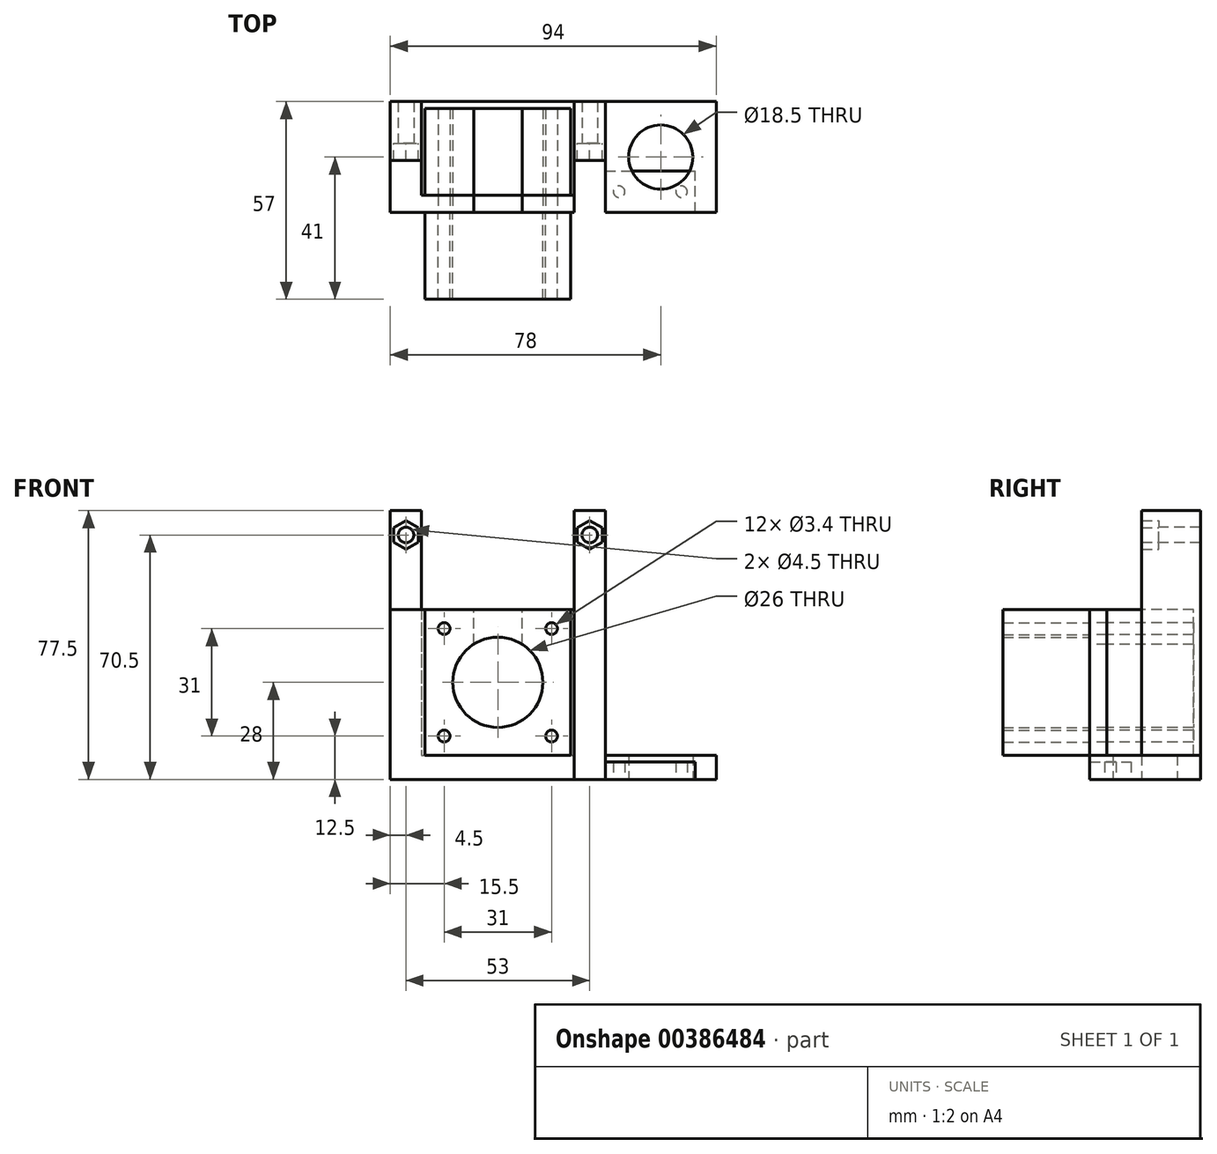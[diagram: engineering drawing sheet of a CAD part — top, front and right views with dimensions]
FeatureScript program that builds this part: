
annotation { "Feature Type Name" : "Feature", "Feature Type Description" : "" }
export const myFeature = defineFeature(function(context is Context, id is Id, definition is map)
    precondition{}
    {
        {
            assignVariable(context, id + "F0", {"name" : "MotorLength", "anyValue" : 25});
        }
        {
            var Q0;
            Q0=qCreatedBy(makeId("Front.planeOp"),FACE);
            var sketch = newSketch(context, id + "F1", { "sketchPlane" : qUnion([Q0])});
            skCircle(sketch, "E0", {"center": v(0, 0) * mm, "radius": 2.25 * mm});
            skCircle(sketch, "E1", {"center": v(-31.5, 49.5) * mm, "radius": 2.25 * mm});
            skCircle(sketch, "E2", {"center": v(21.5, 49.5) * mm, "radius": 2.25 * mm});
            skPoint(sketch, "E3", {"position": v(-36, 56.5) * mm});
            skPoint(sketch, "E4", {"position": v(-27, 56.5) * mm});
            skPoint(sketch, "E5", {"position": v(-27, -14) * mm});
            skLineSegment(sketch, "E6", {"start": v(-36, 56.5) * mm, "end": v(-27, 56.5) * mm});
            skLineSegment(sketch, "E7", {"start": v(-27, 56.5) * mm, "end": v(-27, -14) * mm});
            skLineSegment(sketch, "E8", {"start": v(-27, -14) * mm, "end": v(17, -14) * mm});
            skLineSegment(sketch, "E9", {"start": v(17, -14) * mm, "end": v(17, 56.5) * mm});
            skLineSegment(sketch, "E10", {"start": v(17, 56.5) * mm, "end": v(26, 56.5) * mm});
            skPoint(sketch, "E11", {"position": v(-36, -21) * mm});
            skLineSegment(sketch, "E12", {"start": v(-36, 56.5) * mm, "end": v(-36, -21) * mm});
            skLineSegment(sketch, "E13", {"start": v(-36, -21) * mm, "end": v(26, -21) * mm});
            skLineSegment(sketch, "E14", {"start": v(26, 56.5) * mm, "end": v(26, -21) * mm});
            skSolve(sketch);
        }
        {
            var Q0;
            Q0=makeQuery(id+"F1.imprint","IMPRINT",FACE,{"disambiguationData":[TD([[makeQuery(id+"F1.imprint","IMPRINT",EDGE,{"derivedFrom":sQuery(id+"F1.wireOp",EDGE,"E1")}),-1.0]])]});
            extrude(context, id + "F2", {"entities" : qUnion([Q0]), "oppositeDirection" : true, "depth" : 12 * mm});
        }
        {
            var Q0;
            Q0=makeQuery(id+"F2.opExtrude","CAP_FACE",FACE,{"disambiguationData":[OSD([sQuery(id+"F1.wireOp",EDGE,"E1"),sQuery(id+"F1.wireOp",EDGE,"E2"),sQuery(id+"F1.wireOp",EDGE,"E6"),sQuery(id+"F1.wireOp",EDGE,"E7"),sQuery(id+"F1.wireOp",EDGE,"E8"),sQuery(id+"F1.wireOp",EDGE,"E9"),sQuery(id+"F1.wireOp",EDGE,"E10"),sQuery(id+"F1.wireOp",EDGE,"E12"),sQuery(id+"F1.wireOp",EDGE,"E13"),sQuery(id+"F1.wireOp",EDGE,"E14")])],"isStart":true});
            var sketch = newSketch(context, id + "F3", { "sketchPlane" : qUnion([Q0])});
            skCircle(sketch, "E15.cCircle", {"center": v(-31.5, 49.5) * mm, "radius": 3.6 * mm, "construction": true});
            skLineSegment(sketch, "E15.0", {"start": v(-27.9, 51.58) * mm, "end": v(-27.9, 47.42) * mm});
            skLineSegment(sketch, "E15.1", {"start": v(-27.9, 47.42) * mm, "end": v(-31.5, 45.34) * mm});
            skLineSegment(sketch, "E15.2", {"start": v(-31.5, 45.34) * mm, "end": v(-35.1, 47.42) * mm});
            skLineSegment(sketch, "E15.3", {"start": v(-35.1, 47.42) * mm, "end": v(-35.1, 51.58) * mm});
            skLineSegment(sketch, "E15.4", {"start": v(-35.1, 51.58) * mm, "end": v(-31.5, 53.66) * mm});
            skLineSegment(sketch, "E15.5", {"start": v(-31.5, 53.66) * mm, "end": v(-27.9, 51.58) * mm});
            skPoint(sketch, "E15.0.midPoint", {"position": v(-27.9, 49.5) * mm});
            skCircle(sketch, "E16.cCircle", {"center": v(21.5, 49.5) * mm, "radius": 3.6 * mm, "construction": true});
            skLineSegment(sketch, "E16.0", {"start": v(25.1, 51.58) * mm, "end": v(25.1, 47.42) * mm});
            skLineSegment(sketch, "E16.1", {"start": v(25.1, 47.42) * mm, "end": v(21.5, 45.34) * mm});
            skLineSegment(sketch, "E16.2", {"start": v(21.5, 45.34) * mm, "end": v(17.9, 47.42) * mm});
            skLineSegment(sketch, "E16.3", {"start": v(17.9, 47.42) * mm, "end": v(17.9, 51.58) * mm});
            skLineSegment(sketch, "E16.4", {"start": v(17.9, 51.58) * mm, "end": v(21.5, 53.66) * mm});
            skLineSegment(sketch, "E16.5", {"start": v(21.5, 53.66) * mm, "end": v(25.1, 51.58) * mm});
            skPoint(sketch, "E16.0.midPoint", {"position": v(25.1, 49.5) * mm});
            skSolve(sketch);
        }
        {
            var Q0;
            Q0=makeQuery(id+"F3.imprint","IMPRINT",FACE,{"disambiguationData":[TD([[makeQuery(id+"F3.imprint","IMPRINT",EDGE,{"derivedFrom":sQuery(id+"F3.wireOp",EDGE,"E15.0")}),1.0]])]});
            extrude(context, id + "F4", {"entities" : qUnion([Q0]), "operationType" : NewBodyOperationType.ADD, "depth" : 5 * mm});
        }
        {
            var Q0;
            {var subQ0=sQuery(id+"F1.wireOp",EDGE,"E8");Q0=makeQuery(id+"F4.boolean.opBoolean","MERGE",FACE,{"derivedFrom":[makeQuery(id+"F2.opExtrude","SWEPT_FACE",FACE,{"disambiguationData":[OSD([subQ0])]}),makeQuery(id+"F4.opExtrude","SWEPT_FACE",FACE,{"disambiguationData":[OSD([subQ0])]})]});}
            var sketch = newSketch(context, id + "F5", { "sketchPlane" : qUnion([Q0])});
            skLineSegment(sketch, "E17.0", {"start": v(-27, 12) * mm, "end": v(17, 12) * mm});
            skPoint(sketch, "E18.oppositeSnap0", {"position": v(17, 3.5) * mm});
            skLineSegment(sketch, "E18.top", {"start": v(-27, -15) * mm, "end": v(17, -15) * mm});
            skLineSegment(sketch, "E18.left", {"start": v(-27, 12) * mm, "end": v(-27, -15) * mm});
            skLineSegment(sketch, "E18.right", {"start": v(17, 12) * mm, "end": v(17, -15) * mm});
            skLineSegment(sketch, "E19.top", {"start": v(-27, -20) * mm, "end": v(17, -20) * mm});
            skLineSegment(sketch, "E19.left", {"start": v(-27, -15) * mm, "end": v(-27, -20) * mm});
            skLineSegment(sketch, "E19.right", {"start": v(17, -15) * mm, "end": v(17, -20) * mm});
            skLineSegment(sketch, "E20.0", {"start": v(17, -5) * mm, "end": v(26, -5) * mm});
            skLineSegment(sketch, "E21.bottom", {"start": v(26, -5) * mm, "end": v(17, -5) * mm});
            skLineSegment(sketch, "E21.top", {"start": v(26, -20) * mm, "end": v(17, -20) * mm});
            skLineSegment(sketch, "E21.left", {"start": v(26, -5) * mm, "end": v(26, -20) * mm});
            skLineSegment(sketch, "E21.right", {"start": v(17, -5) * mm, "end": v(17, -20) * mm});
            skLineSegment(sketch, "E22.0", {"start": v(-36, -5) * mm, "end": v(-27, -5) * mm});
            skLineSegment(sketch, "E23.top", {"start": v(-36, -20) * mm, "end": v(-27, -20) * mm});
            skLineSegment(sketch, "E23.left", {"start": v(-36, -5) * mm, "end": v(-36, -20) * mm});
            skLineSegment(sketch, "E23.right", {"start": v(-27, -5) * mm, "end": v(-27, -20) * mm});
            skSolve(sketch);
        }
        {
            var Q0;
            {var subQ0=sQuery(id+"F5.wireOp",EDGE,"E18.top");Q0=makeQuery(id+"F5.imprint","IMPRINT",FACE,{"disambiguationData":[TD([[makeQuery(id+"F5.imprint","IMPRINT",EDGE,{"derivedFrom":subQ0}),1.0]])]});}
            var Q1;
            {var subQ0=sQuery(id+"F5.wireOp",EDGE,"E18.top");Q1=makeQuery(id+"F5.imprint","IMPRINT",FACE,{"disambiguationData":[TD([[makeQuery(id+"F5.imprint","IMPRINT",EDGE,{"derivedFrom":subQ0}),-1.0]])]});}
            var Q2;
            {var subQ1=sQuery(id+"F5.wireOp",EDGE,"E22.0");Q2=makeQuery(id+"F5.imprint","IMPRINT",FACE,{"disambiguationData":[TD([[makeQuery(id+"F5.imprint","IMPRINT",EDGE,{"derivedFrom":subQ1}),-1.0]])]});}
            var Q3;
            {var subQ1=sQuery(id+"F5.wireOp",EDGE,"E21.bottom");Q3=makeQuery(id+"F5.imprint","IMPRINT",FACE,{"disambiguationData":[TD([[makeQuery(id+"F5.imprint","IMPRINT",EDGE,{"derivedFrom":subQ1}),1.0]])]});}
            var Q4;
            {var subQ0=sQuery(id+"F1.wireOp",EDGE,"E13");Q4=makeQuery(id+"F4.boolean.opBoolean","MERGE",FACE,{"derivedFrom":[makeQuery(id+"F2.opExtrude","SWEPT_FACE",FACE,{"disambiguationData":[OSD([subQ0])]}),makeQuery(id+"F4.opExtrude","SWEPT_FACE",FACE,{"disambiguationData":[OSD([subQ0])]})]});}
            extrude(context, id + "F6", {"entities" : qUnion([Q0, Q1, Q2, Q3]), "operationType" : NewBodyOperationType.ADD, "endBound" : BoundingType.UP_TO_SURFACE, "oppositeDirection" : true, "endBoundEntityFace" : qUnion([Q4]), "depth" : 25 * mm});
        }
        {
            var Q0;
            {var subQ0=sQuery(id+"F5.wireOp",EDGE,"E18.top");Q0=makeQuery(id+"F5.imprint","IMPRINT",FACE,{"disambiguationData":[TD([[makeQuery(id+"F5.imprint","IMPRINT",EDGE,{"derivedFrom":subQ0}),-1.0]])]});}
            var Q1;
            {var subQ1=sQuery(id+"F5.wireOp",EDGE,"E22.0");Q1=makeQuery(id+"F5.imprint","IMPRINT",FACE,{"disambiguationData":[TD([[makeQuery(id+"F5.imprint","IMPRINT",EDGE,{"derivedFrom":subQ1}),-1.0]])]});}
            var Q2;
            {var subQ1=sQuery(id+"F5.wireOp",EDGE,"E21.bottom");Q2=makeQuery(id+"F5.imprint","IMPRINT",FACE,{"disambiguationData":[TD([[makeQuery(id+"F5.imprint","IMPRINT",EDGE,{"derivedFrom":subQ1}),1.0]])]});}
            extrude(context, id + "F7", {"entities" : qUnion([Q0, Q1, Q2]), "operationType" : NewBodyOperationType.ADD, "depth" : 42 * mm});
        }
        {
            var Q0;
            {var subQ0=sQuery(id+"F5.wireOp",EDGE,"E23.top");var subQ1=sQuery(id+"F5.wireOp",EDGE,"E21.top");var subQ2=sQuery(id+"F5.wireOp",EDGE,"E19.top");Q0=makeQuery(id+"F7.boolean.opBoolean","MERGE",FACE,{"derivedFrom":[makeQuery(id+"F6.opExtrude","SWEPT_FACE",FACE,{"disambiguationData":[OSD([subQ2,subQ1,subQ0])]}),makeQuery(id+"F7.opExtrude","SWEPT_FACE",FACE,{"disambiguationData":[OSD([subQ2,subQ1,subQ0])]})]});}
            var sketch = newSketch(context, id + "F8", { "sketchPlane" : qUnion([Q0])});
            skLineSegment(sketch, "E24.0", {"start": v(-26, -14) * mm, "end": v(16, -14) * mm});
            skPoint(sketch, "E25", {"position": v(-5, -14) * mm});
            skPoint(sketch, "E26", {"position": v(-26, -14) * mm});
            skPoint(sketch, "E27", {"position": v(16, -14) * mm});
            skPoint(sketch, "E28.orphan", {"position": v(-27, -14) * mm});
            skPoint(sketch, "E29.orphan", {"position": v(17, -14) * mm});
            skPoint(sketch, "E30", {"position": v(-26, 28) * mm});
            skPoint(sketch, "E31", {"position": v(16, 28) * mm});
            skLineSegment(sketch, "E32", {"start": v(-26, 28) * mm, "end": v(16, -14) * mm, "construction": true});
            skLineSegment(sketch, "E33", {"start": v(-26, -14) * mm, "end": v(16, 28) * mm, "construction": true});
            skPoint(sketch, "E34", {"position": v(-5, 7) * mm});
            skCircle(sketch, "E35", {"center": v(-5, 7) * mm, "radius": 13 * mm});
            skCircle(sketch, "E36", {"center": v(-20.5, 22.5) * mm, "radius": 1.7 * mm});
            skCircle(sketch, "E37.1.0", {"center": v(-20.5, -8.5) * mm, "radius": 1.7 * mm});
            skCircle(sketch, "E37.2.0", {"center": v(10.5, -8.5) * mm, "radius": 1.7 * mm});
            skCircle(sketch, "E37.3.0", {"center": v(10.5, 22.5) * mm, "radius": 1.7 * mm});
            skSolve(sketch);
        }
        {
            var Q0;
            Q0=makeQuery(id+"F8.imprint","IMPRINT",FACE,{"disambiguationData":[TD([[makeQuery(id+"F8.imprint","IMPRINT",EDGE,{"derivedFrom":sQuery(id+"F8.wireOp",EDGE,"E36")}),1.0]])]});
            var Q1;
            Q1=makeQuery(id+"F8.imprint","IMPRINT",FACE,{"disambiguationData":[TD([[makeQuery(id+"F8.imprint","IMPRINT",EDGE,{"derivedFrom":sQuery(id+"F8.wireOp",EDGE,"E35")}),1.0]])]});
            var Q2;
            Q2=makeQuery(id+"F8.imprint","IMPRINT",FACE,{"disambiguationData":[TD([[makeQuery(id+"F8.imprint","IMPRINT",EDGE,{"derivedFrom":sQuery(id+"F8.wireOp",EDGE,"E37.1.0")}),1.0]])]});
            var Q3;
            Q3=makeQuery(id+"F8.imprint","IMPRINT",FACE,{"disambiguationData":[TD([[makeQuery(id+"F8.imprint","IMPRINT",EDGE,{"derivedFrom":sQuery(id+"F8.wireOp",EDGE,"E37.2.0")}),1.0]])]});
            var Q4;
            Q4=makeQuery(id+"F8.imprint","IMPRINT",FACE,{"disambiguationData":[TD([[makeQuery(id+"F8.imprint","IMPRINT",EDGE,{"derivedFrom":sQuery(id+"F8.wireOp",EDGE,"E37.3.0")}),1.0]])]});
            var Q5;
            Q5=makeQuery(id+"F7.opExtrude","SWEPT_FACE",FACE,{"disambiguationData":[OSD([sQuery(id+"F5.wireOp",EDGE,"E18.top")])]});
            extrude(context, id + "F9", {"entities" : qUnion([Q0, Q1, Q2, Q3, Q4]), "operationType" : NewBodyOperationType.REMOVE, "endBound" : BoundingType.UP_TO_SURFACE, "oppositeDirection" : true, "endBoundEntityFace" : qUnion([Q5]), "depth" : 25 * mm});
        }
        {
            var Q0;
            Q0=makeQuery(id+"F7.opExtrude","CAP_FACE",FACE,{"disambiguationData":[OSD([sQuery(id+"F5.wireOp",EDGE,"E18.top"),sQuery(id+"F5.wireOp",EDGE,"E19.top"),sQuery(id+"F5.wireOp",EDGE,"E21.bottom"),sQuery(id+"F5.wireOp",EDGE,"E21.top"),sQuery(id+"F5.wireOp",EDGE,"E21.left"),sQuery(id+"F5.wireOp",EDGE,"E21.right"),sQuery(id+"F5.wireOp",EDGE,"E22.0"),sQuery(id+"F5.wireOp",EDGE,"E23.top"),sQuery(id+"F5.wireOp",EDGE,"E23.left"),sQuery(id+"F5.wireOp",EDGE,"E23.right")])],"isStart":false});
            var sketch = newSketch(context, id + "F10", { "sketchPlane" : qUnion([Q0])});
            skLineSegment(sketch, "E38", {"start": v(-5, -20) * mm, "end": v(-5, -15) * mm, "construction": true});
            skLineSegment(sketch, "E39", {"start": v(-5, -15) * mm, "end": v(-12, -15) * mm});
            skLineSegment(sketch, "E40", {"start": v(-5, -15) * mm, "end": v(2, -15) * mm});
            skLineSegment(sketch, "E41.bottom", {"start": v(-12, -15) * mm, "end": v(2, -15) * mm});
            skLineSegment(sketch, "E41.top", {"start": v(-12, -20) * mm, "end": v(2, -20) * mm});
            skLineSegment(sketch, "E41.left", {"start": v(-12, -15) * mm, "end": v(-12, -20) * mm});
            skLineSegment(sketch, "E41.right", {"start": v(2, -15) * mm, "end": v(2, -20) * mm});
            skSolve(sketch);
        }
        {
            var Q0;
            Q0=makeQuery(id+"F10.imprint","IMPRINT",FACE,{"disambiguationData":[TD([[makeQuery(id+"F10.imprint","IMPRINT",EDGE,{"derivedFrom":sQuery(id+"F10.wireOp",EDGE,"E41.top")}),1.0]])]});
            var Q1;
            Q1=makeQuery(id+"F9.boolean.opBoolean","COPY",FACE,{"derivedFrom":makeQuery(id+"F9.opExtrude","SWEPT_FACE",FACE,{"disambiguationData":[OSD([sQuery(id+"F8.wireOp",EDGE,"E35")])]})});
            extrude(context, id + "F11", {"entities" : qUnion([Q0]), "operationType" : NewBodyOperationType.REMOVE, "endBound" : BoundingType.UP_TO_SURFACE, "oppositeDirection" : true, "endBoundEntityFace" : qUnion([Q1]), "depth" : 25 * mm});
        }
        {
            var Q0;
            Q0=makeQuery(id+"F7.opExtrude","SWEPT_FACE",FACE,{"disambiguationData":[OSD([sQuery(id+"F5.wireOp",EDGE,"E18.top")])]});
            var sketch = newSketch(context, id + "F12", { "sketchPlane" : qUnion([Q0])});
            skLineSegment(sketch, "E42.0", {"start": v(26, -14) * mm, "end": v(-16, -14) * mm});
            skLineSegment(sketch, "E43", {"start": v(-16, -14) * mm, "end": v(-16, 28) * mm});
            skLineSegment(sketch, "E44", {"start": v(-16, 28) * mm, "end": v(26, 28) * mm});
            skLineSegment(sketch, "E45", {"start": v(26, 28) * mm, "end": v(26, -14) * mm});
            skSolve(sketch);
        }
        {
            var Q0;
            Q0=makeQuery(id+"F12.imprint","IMPRINT",FACE,{"disambiguationData":[TD([[makeQuery(id+"F12.imprint","IMPRINT",EDGE,{"derivedFrom":sQuery(id+"F12.wireOp",EDGE,"E42.0")}),-1.0]])]});
            var Q1;
            Q1=makeQuery(id+"F12.imprint","IMPRINT",FACE,{"disambiguationData":[TD([[makeQuery(id+"F12.imprint","IMPRINT",EDGE,{"derivedFrom":makeQuery(id+"F9.boolean.opBoolean","COPY",EDGE,{"derivedFrom":makeQuery(id+"F9.opExtrude","CAP_EDGE",EDGE,{"disambiguationData":[OSD([sQuery(id+"F8.wireOp",EDGE,"E35")])],"isStart":false})})}),-1.0]])]});
            var Q2;
            Q2=makeQuery(id+"F12.imprint","IMPRINT",FACE,{"disambiguationData":[TD([[makeQuery(id+"F12.imprint","IMPRINT",EDGE,{"derivedFrom":makeQuery(id+"F9.boolean.opBoolean","COPY",EDGE,{"derivedFrom":makeQuery(id+"F9.opExtrude","CAP_EDGE",EDGE,{"disambiguationData":[OSD([sQuery(id+"F8.wireOp",EDGE,"E36")])],"isStart":false})})}),-1.0]])]});
            var Q3;
            Q3=makeQuery(id+"F12.imprint","IMPRINT",FACE,{"disambiguationData":[TD([[makeQuery(id+"F12.imprint","IMPRINT",EDGE,{"derivedFrom":makeQuery(id+"F9.boolean.opBoolean","COPY",EDGE,{"derivedFrom":makeQuery(id+"F9.opExtrude","CAP_EDGE",EDGE,{"disambiguationData":[OSD([sQuery(id+"F8.wireOp",EDGE,"E37.3.0")])],"isStart":false})})}),-1.0]])]});
            var Q4;
            Q4=makeQuery(id+"F12.imprint","IMPRINT",FACE,{"disambiguationData":[TD([[makeQuery(id+"F12.imprint","IMPRINT",EDGE,{"derivedFrom":makeQuery(id+"F9.boolean.opBoolean","COPY",EDGE,{"derivedFrom":makeQuery(id+"F9.opExtrude","CAP_EDGE",EDGE,{"disambiguationData":[OSD([sQuery(id+"F8.wireOp",EDGE,"E37.2.0")])],"isStart":false})})}),-1.0]])]});
            var Q5;
            Q5=makeQuery(id+"F12.imprint","IMPRINT",FACE,{"disambiguationData":[TD([[makeQuery(id+"F12.imprint","IMPRINT",EDGE,{"derivedFrom":makeQuery(id+"F9.boolean.opBoolean","COPY",EDGE,{"derivedFrom":makeQuery(id+"F9.opExtrude","CAP_EDGE",EDGE,{"disambiguationData":[OSD([sQuery(id+"F8.wireOp",EDGE,"E37.1.0")])],"isStart":false})})}),-1.0]])]});
            extrude(context, id + "F13", {"entities" : qUnion([Q0, Q1, Q2, Q3, Q4, Q5]), "depth" : (getVariable(context, 'MotorLength')) * mm});
        }
        {
            var Q0;
            Q0=makeQuery(id+"F8.imprint","IMPRINT",FACE,{"disambiguationData":[TD([[makeQuery(id+"F8.imprint","IMPRINT",EDGE,{"derivedFrom":sQuery(id+"F8.wireOp",EDGE,"E35")}),-1.0]])]});
            var sketch = newSketch(context, id + "F14", { "sketchPlane" : qUnion([Q0])});
            skLineSegment(sketch, "E46.0", {"start": v(-26, 28) * mm, "end": v(16, -14) * mm, "construction": true});
            skLineSegment(sketch, "E47.0", {"start": v(-26, -14) * mm, "end": v(16, 28) * mm, "construction": true});
            skLineSegment(sketch, "E48.bottom", {"start": v(-26, 28) * mm, "end": v(16, 28) * mm});
            skLineSegment(sketch, "E48.top", {"start": v(-26, -14) * mm, "end": v(16, -14) * mm});
            skLineSegment(sketch, "E48.left", {"start": v(-26, 28) * mm, "end": v(-26, -14) * mm});
            skLineSegment(sketch, "E48.right", {"start": v(16, 28) * mm, "end": v(16, -14) * mm});
            skSolve(sketch);
        }
        {
            var Q0;
            Q0=makeQuery(id+"F14.imprint","IMPRINT",FACE,{"disambiguationData":[TD([[makeQuery(id+"F14.imprint","IMPRINT",EDGE,{"derivedFrom":sQuery(id+"F14.wireOp",EDGE,"E48.bottom")}),-1.0]])]});
            var Q1;
            Q1=makeQuery(id+"F8.imprint","IMPRINT",FACE,{"disambiguationData":[TD([[makeQuery(id+"F8.imprint","IMPRINT",EDGE,{"derivedFrom":sQuery(id+"F8.wireOp",EDGE,"E36")}),1.0]])]});
            var Q2;
            Q2=makeQuery(id+"F8.imprint","IMPRINT",FACE,{"disambiguationData":[TD([[makeQuery(id+"F8.imprint","IMPRINT",EDGE,{"derivedFrom":sQuery(id+"F8.wireOp",EDGE,"E35")}),1.0]])]});
            var Q3;
            Q3=makeQuery(id+"F8.imprint","IMPRINT",FACE,{"disambiguationData":[TD([[makeQuery(id+"F8.imprint","IMPRINT",EDGE,{"derivedFrom":sQuery(id+"F8.wireOp",EDGE,"E37.1.0")}),1.0]])]});
            var Q4;
            Q4=makeQuery(id+"F8.imprint","IMPRINT",FACE,{"disambiguationData":[TD([[makeQuery(id+"F8.imprint","IMPRINT",EDGE,{"derivedFrom":sQuery(id+"F8.wireOp",EDGE,"E37.3.0")}),1.0]])]});
            var Q5;
            Q5=makeQuery(id+"F8.imprint","IMPRINT",FACE,{"disambiguationData":[TD([[makeQuery(id+"F8.imprint","IMPRINT",EDGE,{"derivedFrom":sQuery(id+"F8.wireOp",EDGE,"E37.2.0")}),1.0]])]});
            extrude(context, id + "F15", {"entities" : qUnion([Q0, Q1, Q2, Q3, Q4, Q5]), "depth" : 25 * mm});
        }
        {
            var Q0;
            {var subQ0=sQuery(id+"F1.wireOp",EDGE,"E13");Q0=makeQuery(id+"F6.boolean.opBoolean","MERGE",FACE,{"derivedFrom":[makeQuery(id+"F4.boolean.opBoolean","MERGE",FACE,{"derivedFrom":[makeQuery(id+"F2.opExtrude","SWEPT_FACE",FACE,{"disambiguationData":[OSD([subQ0])]}),makeQuery(id+"F4.opExtrude","SWEPT_FACE",FACE,{"disambiguationData":[OSD([subQ0])]})]}),makeQuery(id+"F6.opExtrude","CAP_FACE",FACE,{"disambiguationData":[OSD([sQuery(id+"F1.wireOp",EDGE,"E8"),sQuery(id+"F5.wireOp",EDGE,"E19.top"),sQuery(id+"F5.wireOp",EDGE,"E21.bottom"),sQuery(id+"F5.wireOp",EDGE,"E21.top"),sQuery(id+"F5.wireOp",EDGE,"E21.left"),sQuery(id+"F5.wireOp",EDGE,"E22.0"),sQuery(id+"F5.wireOp",EDGE,"E23.top"),sQuery(id+"F5.wireOp",EDGE,"E23.left")])],"isStart":false})]});}
            var sketch = newSketch(context, id + "F16", { "sketchPlane" : qUnion([Q0])});
            skLineSegment(sketch, "E49.bottom", {"start": v(26, -12) * mm, "end": v(58, -12) * mm});
            skLineSegment(sketch, "E49.top", {"start": v(26, 20) * mm, "end": v(58, 20) * mm});
            skLineSegment(sketch, "E49.left", {"start": v(26, -12) * mm, "end": v(26, 20) * mm});
            skLineSegment(sketch, "E49.right", {"start": v(58, -12) * mm, "end": v(58, 20) * mm});
            skCircle(sketch, "E50", {"center": v(42, 4) * mm, "radius": 9.25 * mm});
            skPoint(sketch, "E50.centerSnap0", {"position": v(42, -12) * mm});
            skPoint(sketch, "E50.centerSnap1", {"position": v(26, 4) * mm});
            skLineSegment(sketch, "E51.0", {"start": v(-26, 45) * mm, "end": v(-26, 20) * mm, "construction": true});
            skLineSegment(sketch, "E52.0", {"start": v(-26, 20) * mm, "end": v(16, 20) * mm, "construction": true});
            skLineSegment(sketch, "E53", {"start": v(-5, 20) * mm, "end": v(-5, 45) * mm, "construction": true});
            skLineSegment(sketch, "E54", {"start": v(6.1, 20) * mm, "end": v(6.1, 45) * mm, "construction": true});
            skPoint(sketch, "E55", {"position": v(6.1, 32.5) * mm});
            skSolve(sketch);
        }
        {
            var Q0;
            Q0=qSketchRegion(id+"F16",true);
            var Q1;
            {var subQ0=sQuery(id+"F1.wireOp",EDGE,"E8");Q1=makeQuery(id+"F6.boolean.opBoolean","MERGE",FACE,{"derivedFrom":[makeQuery(id+"F4.boolean.opBoolean","MERGE",FACE,{"derivedFrom":[makeQuery(id+"F2.opExtrude","SWEPT_FACE",FACE,{"disambiguationData":[OSD([subQ0])]}),makeQuery(id+"F4.opExtrude","SWEPT_FACE",FACE,{"disambiguationData":[OSD([subQ0])]})]}),makeQuery(id+"F6.opExtrude","CAP_FACE",FACE,{"disambiguationData":[OSD([subQ0,sQuery(id+"F5.wireOp",EDGE,"E19.top"),sQuery(id+"F5.wireOp",EDGE,"E21.bottom"),sQuery(id+"F5.wireOp",EDGE,"E21.top"),sQuery(id+"F5.wireOp",EDGE,"E21.left"),sQuery(id+"F5.wireOp",EDGE,"E22.0"),sQuery(id+"F5.wireOp",EDGE,"E23.top"),sQuery(id+"F5.wireOp",EDGE,"E23.left")])],"isStart":true})]});}
            extrude(context, id + "F17", {"entities" : qUnion([Q0]), "endBound" : BoundingType.UP_TO_SURFACE, "oppositeDirection" : true, "endBoundEntityFace" : qUnion([Q1]), "depth" : 25 * mm});
        }
        {
            var Q0;
            {var subQ0=sQuery(id+"F1.wireOp",EDGE,"E13");Q0=makeQuery(id+"F6.boolean.opBoolean","MERGE",FACE,{"derivedFrom":[makeQuery(id+"F4.boolean.opBoolean","MERGE",FACE,{"derivedFrom":[makeQuery(id+"F2.opExtrude","SWEPT_FACE",FACE,{"disambiguationData":[OSD([subQ0])]}),makeQuery(id+"F4.opExtrude","SWEPT_FACE",FACE,{"disambiguationData":[OSD([subQ0])]})]}),makeQuery(id+"F6.opExtrude","CAP_FACE",FACE,{"disambiguationData":[OSD([sQuery(id+"F1.wireOp",EDGE,"E8"),sQuery(id+"F5.wireOp",EDGE,"E19.top"),sQuery(id+"F5.wireOp",EDGE,"E21.bottom"),sQuery(id+"F5.wireOp",EDGE,"E21.top"),sQuery(id+"F5.wireOp",EDGE,"E21.left"),sQuery(id+"F5.wireOp",EDGE,"E22.0"),sQuery(id+"F5.wireOp",EDGE,"E23.top"),sQuery(id+"F5.wireOp",EDGE,"E23.left")])],"isStart":false})]});}
            var sketch = newSketch(context, id + "F18", { "sketchPlane" : qUnion([Q0])});
            skLineSegment(sketch, "E56.bottom", {"start": v(26, 20) * mm, "end": v(52, 20) * mm});
            skLineSegment(sketch, "E56.top", {"start": v(26, 8) * mm, "end": v(52, 8) * mm});
            skLineSegment(sketch, "E56.left", {"start": v(26, 20) * mm, "end": v(26, 8) * mm});
            skLineSegment(sketch, "E56.right", {"start": v(52, 20) * mm, "end": v(52, 8) * mm});
            skLineSegment(sketch, "E57", {"start": v(39, 20) * mm, "end": v(39, 8) * mm, "construction": true});
            skPoint(sketch, "E58", {"position": v(30, 14) * mm});
            skPoint(sketch, "E58.positionSnap0", {"position": v(39, 14) * mm});
            skPoint(sketch, "E59.MirrorP", {"position": v(48, 14) * mm});
            skSolve(sketch);
        }
        {
            var Q0;
            Q0=makeQuery(id+"F18.imprint","IMPRINT",FACE,{"disambiguationData":[TD([[makeQuery(id+"F18.imprint","IMPRINT",EDGE,{"derivedFrom":sQuery(id+"F18.wireOp",EDGE,"E56.bottom")}),-1.0]])]});
            extrude(context, id + "F19", {"entities" : qUnion([Q0]), "oppositeDirection" : true, "depth" : 5 * mm});
        }
        {
            var Q0;
            Q0=sQuery(id+"F18.wireOp",VERTEX,"E58");
            var Q1;
            Q1=sQuery(id+"F18.wireOp",VERTEX,"E59.MirrorP");
            var Q2;
            Q2=makeQuery(id+"F19.opExtrude","SWEPT_BODY",BODY,{"disambiguationData":[OSD([sQuery(id+"F18.wireOp",EDGE,"E56.bottom"),sQuery(id+"F18.wireOp",EDGE,"E56.top"),sQuery(id+"F18.wireOp",EDGE,"E56.left"),sQuery(id+"F18.wireOp",EDGE,"E56.right")])]});
            hole(context, id + "F20", {"style" : HoleStyle.SIMPLE, "endStyle" : HoleEndStyle.THROUGH, "standardTappedOrClearance" : lookupTablePath({ "standard" : "ISO", "fit" : "Normal", "size" : "M3", "type" : "Clearance" }), "standardBlindInLast" : lookupTablePath({ "fit" : "Standard", "standard" : "ISO", "size" : "M3", "type" : "Clearance" }), "holeDiameter" : 3.3 * mm, "isTappedThrough" : true, "tappedDepth" : 12 * mm, "tapClearance" : 3, "startFromSketch" : true, "locations" : qUnion([Q0, Q1]), "scope" : qUnion([Q2])});
        }
    });
